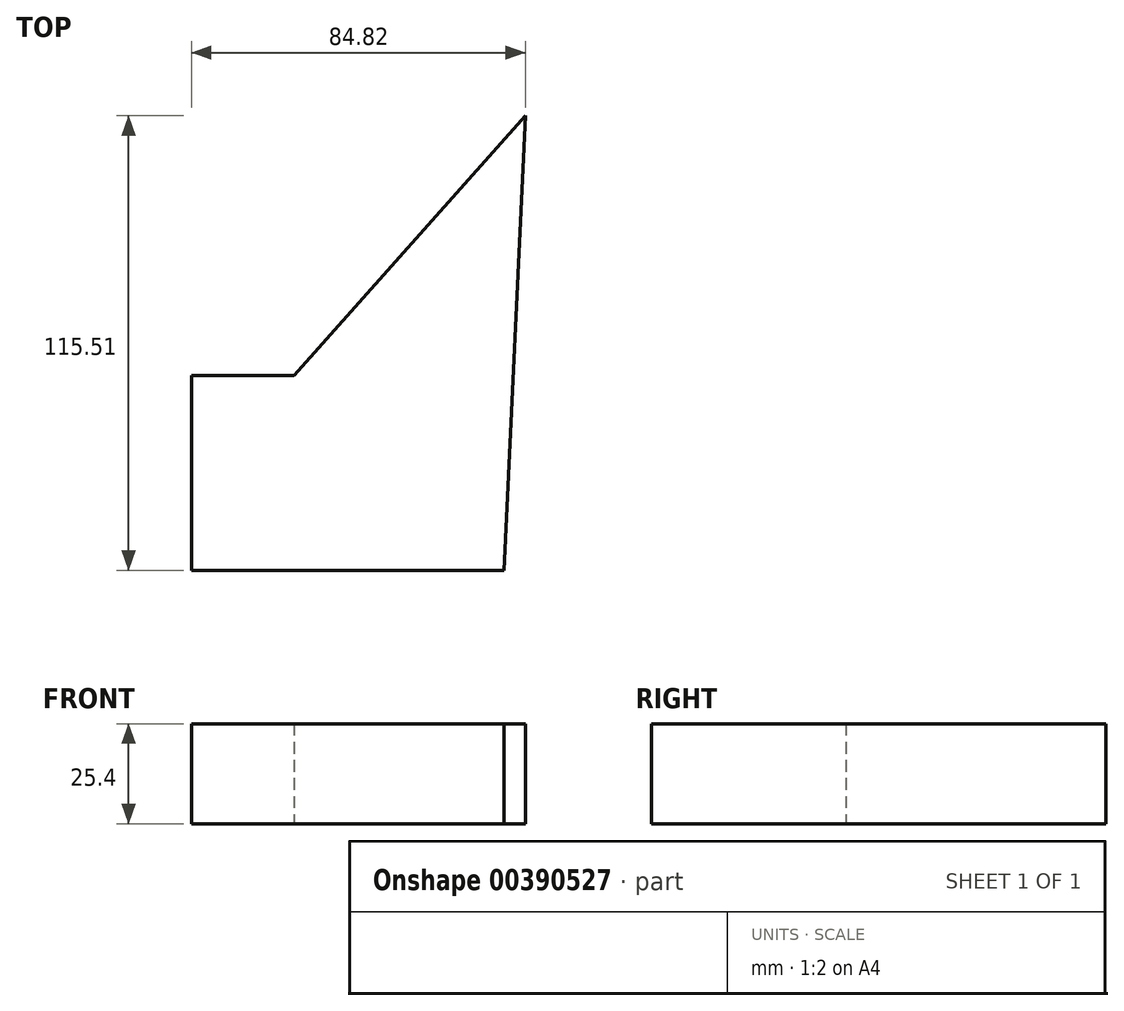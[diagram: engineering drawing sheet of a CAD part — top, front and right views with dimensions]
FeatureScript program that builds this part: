
annotation { "Feature Type Name" : "Feature", "Feature Type Description" : "" }
export const myFeature = defineFeature(function(context is Context, id is Id, definition is map)
    precondition{}
    {
        {
            var Q0;
            Q0=qCreatedBy(makeId("Top.planeOp"),FACE);
            var sketch = newSketch(context, id + "F0", { "sketchPlane" : qUnion([Q0])});
            skLineSegment(sketch, "E0", {"start": v(26.13, 29.39) * mm, "end": v(84.82, 95.4) * mm});
            skLineSegment(sketch, "E1.bottom", {"start": v(79.4, -20.1) * mm, "end": v(0, -20.1) * mm});
            skLineSegment(sketch, "E1.top", {"start": v(26.13, 29.39) * mm, "end": v(0, 29.39) * mm});
            skLineSegment(sketch, "E1.right", {"start": v(0, -20.1) * mm, "end": v(0, 29.39) * mm});
            skPoint(sketch, "E2.orphan", {"position": v(0, 0) * mm});
            skLineSegment(sketch, "E3", {"start": v(79.4, -20.1) * mm, "end": v(84.82, 95.4) * mm});
            skSolve(sketch);
        }
        {
            var Q0;
            Q0 = qSketchRegion(id + "F0", true);
            extrude(context, id + "F1", {"entities" : qUnion([Q0]), "depth" : 25.4 * mm});
        }
    });
